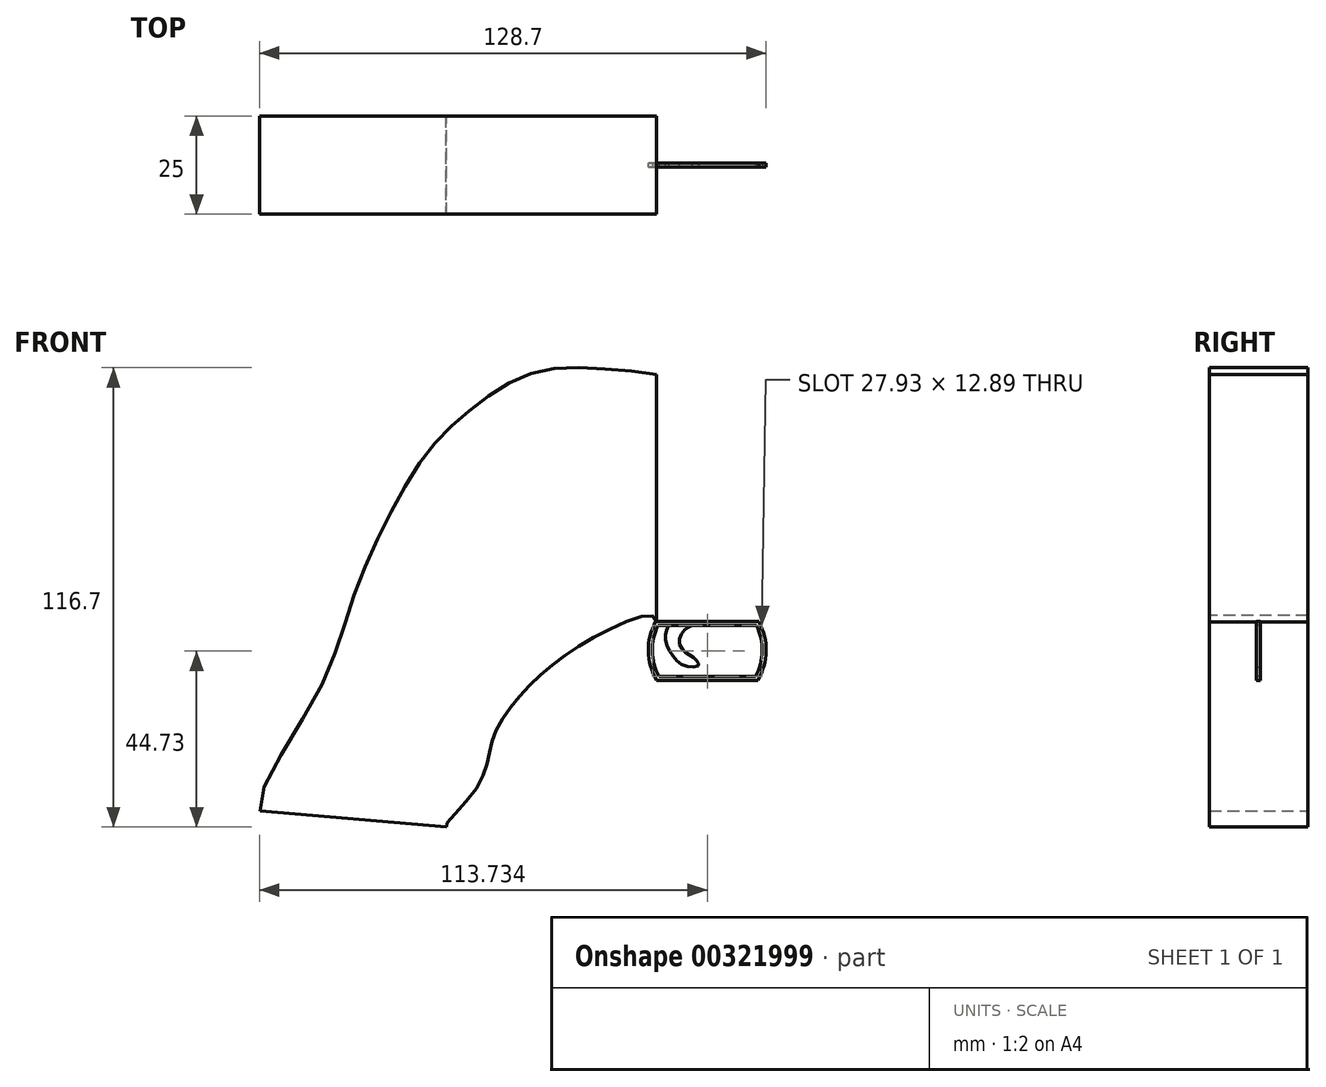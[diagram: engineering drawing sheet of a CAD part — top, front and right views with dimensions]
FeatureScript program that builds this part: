
annotation { "Feature Type Name" : "Feature", "Feature Type Description" : "" }
export const myFeature = defineFeature(function(context is Context, id is Id, definition is map)
    precondition{}
    {
        {
            var Q0;
            Q0=qCreatedBy(makeId("Front.planeOp"),FACE);
            var sketch = newSketch(context, id + "F0", { "sketchPlane" : qUnion([Q0])});
            skLineSegment(sketch, "E0", {"start": v(0, 0) * mm, "end": v(0, 62.77) * mm});
            skFitSpline(sketch, "E1", {"points": [v(0, 62.77) * mm, v(-17.8, 64.5) * mm, v(-33.02, 62.77) * mm, v(-46.17, 54.72) * mm, v(-56.78, 44.86) * mm, v(-67.3, 28.37) * mm, v(-77, 6.33) * mm, v(-86.82, -19.37) * mm, v(-100.72, -48.04) * mm], "startDerivative": vector(-142.89, 24.1) * mm, "endDerivative": vector(31.07, -106.52) * mm});
            skFitSpline(sketch, "E2", {"points": [v(0, 0) * mm, v(-13.24, -2.54) * mm, v(-32.1, -16) * mm, v(-41.6, -29.62) * mm, v(-45.81, -42.27) * mm, v(-53.25, -52.17) * mm], "startDerivative": vector(0, 54.95) * mm, "endDerivative": vector(33.9, 0) * mm});
            skLineSegment(sketch, "E3", {"start": v(-100.72, -48.04) * mm, "end": v(-53.25, -52.17) * mm});
            skSolve(sketch);
        }
        {
            var Q0;
            Q0=makeQuery(id+"F0.imprint","IMPRINT",FACE,{"disambiguationData":[TD([[makeQuery(id+"F0.imprint","IMPRINT",EDGE,{"derivedFrom":sQuery(id+"F0.wireOp",EDGE,"E0")}),1.0]])]});
            extrude(context, id + "F1", {"entities" : qUnion([Q0]), "depth" : 25 * mm});
        }
        {
            var Q0;
            Q0=qCreatedBy(makeId("Front.planeOp"),FACE);
            var sketch = newSketch(context, id + "F2", { "sketchPlane" : qUnion([Q0])});
            skPoint(sketch, "E4.centerSnap0", {"position": v(12.83, -0.46) * mm});
            skArc(sketch, "E5.0", {"start": v(-0.3, 0.02) * mm, "mid": v(-2.13, -7.47) * mm, "end": v(0, -14.88) * mm});
            skLineSegment(sketch, "E5.1", {"start": v(0, -14.88) * mm, "end": v(25.67, -14.88) * mm});
            skArc(sketch, "E5.2", {"start": v(25.97, 0.02) * mm, "mid": v(27.8, -7.47) * mm, "end": v(25.67, -14.88) * mm});
            skLineSegment(sketch, "E6", {"start": v(25.97, 0.02) * mm, "end": v(-0.3, 0.02) * mm});
            skSolve(sketch);
        }
        {
            var Q0;
            Q0=makeQuery(id+"F2.imprint","IMPRINT",FACE,{"disambiguationData":[TD([[makeQuery(id+"F2.imprint","IMPRINT",EDGE,{"derivedFrom":sQuery(id+"F2.wireOp",EDGE,"E5.0")}),1.0]])]});
            extrude(context, id + "F3", {"entities" : qUnion([Q0]), "depth" : 1 * mm});
        }
        {
            var Q0;
            Q0=makeQuery(id+"F3.opExtrude","SWEPT_BODY",BODY,{"disambiguationData":[OSD([sQuery(id+"F2.wireOp",EDGE,"E5.0"),sQuery(id+"F2.wireOp",EDGE,"E5.1"),sQuery(id+"F2.wireOp",EDGE,"E5.2"),sQuery(id+"F2.wireOp",EDGE,"E6")])]});
            transform(context, id + "F4", {"entities" : qUnion([Q0]), "transformType" : TransformType.TRANSLATION_3D, "dx" : 0 * mm, "dy" : -12 * mm, "dz" : 0 * mm, "makeCopy" : false});
        }
        {
            var Q0;
            Q0=makeQuery(id+"F3.opExtrude","CAP_FACE",FACE,{"disambiguationData":[OSD([sQuery(id+"F2.wireOp",EDGE,"E5.0"),sQuery(id+"F2.wireOp",EDGE,"E5.1"),sQuery(id+"F2.wireOp",EDGE,"E5.2"),sQuery(id+"F2.wireOp",EDGE,"E6")])],"isStart":false});
            var sketch = newSketch(context, id + "F5", { "sketchPlane" : qUnion([Q0])});
            skArc(sketch, "E7.0", {"start": v(25.09, -13.88) * mm, "mid": v(26.8, -7.46) * mm, "end": v(25.36, -0.98) * mm});
            skLineSegment(sketch, "E7.1", {"start": v(0.58, -13.88) * mm, "end": v(25.09, -13.88) * mm});
            skArc(sketch, "E7.2", {"start": v(0.3, -0.98) * mm, "mid": v(-1.13, -7.46) * mm, "end": v(0.58, -13.88) * mm});
            skLineSegment(sketch, "E7.3", {"start": v(25.36, -0.98) * mm, "end": v(0.3, -0.98) * mm});
            skSolve(sketch);
        }
        {
            var Q0;
            Q0=makeQuery(id+"F5.imprint","IMPRINT",FACE,{"disambiguationData":[TD([[makeQuery(id+"F5.imprint","IMPRINT",EDGE,{"derivedFrom":sQuery(id+"F5.wireOp",EDGE,"E7.0")}),1.0]])]});
            extrude(context, id + "F6", {"entities" : qUnion([Q0]), "operationType" : NewBodyOperationType.REMOVE, "endBound" : BoundingType.THROUGH_ALL, "oppositeDirection" : true, "depth" : 25 * mm});
        }
        {
            var Q0;
            Q0=makeQuery(id+"F3.opExtrude","CAP_FACE",FACE,{"disambiguationData":[OSD([sQuery(id+"F2.wireOp",EDGE,"E5.0"),sQuery(id+"F2.wireOp",EDGE,"E5.1"),sQuery(id+"F2.wireOp",EDGE,"E5.2"),sQuery(id+"F2.wireOp",EDGE,"E6")])],"isStart":false});
            var sketch = newSketch(context, id + "F7", { "sketchPlane" : qUnion([Q0])});
            skFitSpline(sketch, "E8", {"points": [v(2.95, -0.98) * mm, v(2.23, -4.14) * mm, v(3.76, -8.22) * mm, v(7.39, -11.26) * mm, v(10.63, -11.1) * mm, v(9.99, -9.72) * mm, v(8.02, -8.22) * mm, v(5.8, -5.7) * mm, v(6.77, -2.4) * mm, v(8.95, -0.98) * mm], "startDerivative": vector(-11.37, -26.53) * mm, "endDerivative": vector(22.92, 9.16) * mm});
            skSolve(sketch);
        }
        {
            var Q0;
            {var subQ0=sQuery(id+"F7.wireOp",EDGE,"E8");Q0=makeQuery(id+"F7.imprint","IMPRINT",FACE,{"disambiguationData":[TD([[makeQuery(id+"F7.imprint","IMPRINT",EDGE,{"derivedFrom":subQ0}),1.0]])]});}
            extrude(context, id + "F8", {"entities" : qUnion([Q0]), "oppositeDirection" : true, "depth" : 1 * mm});
        }
    });
